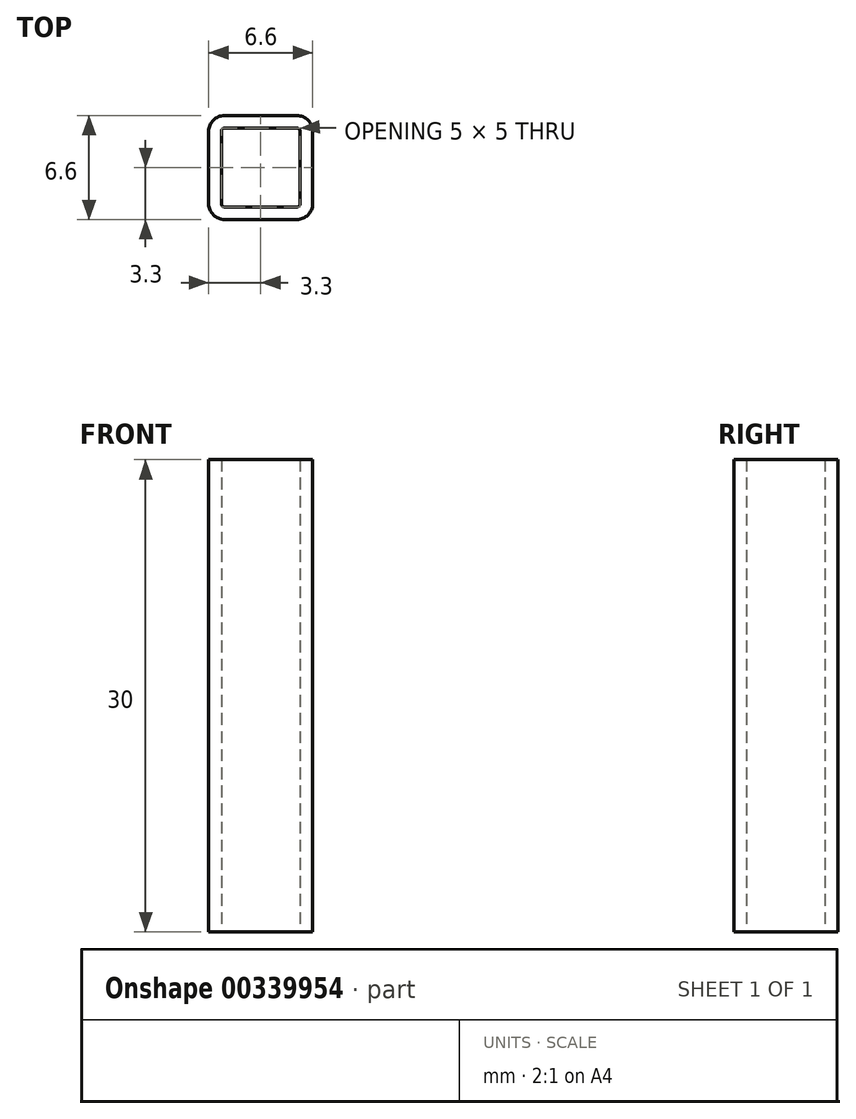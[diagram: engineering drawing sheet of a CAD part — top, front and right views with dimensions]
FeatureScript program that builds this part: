
annotation { "Feature Type Name" : "Feature", "Feature Type Description" : "" }
export const myFeature = defineFeature(function(context is Context, id is Id, definition is map)
    precondition{}
    {
        {
            var Q0;
            Q0=qCreatedBy(makeId("Top.planeOp"),FACE);
            var sketch = newSketch(context, id + "F0", { "sketchPlane" : qUnion([Q0])});
            skLineSegment(sketch, "E0.bottom", {"start": v(2.5, -2.5) * mm, "end": v(-2.5, -2.5) * mm});
            skLineSegment(sketch, "E0.top", {"start": v(2.5, 2.5) * mm, "end": v(-2.5, 2.5) * mm});
            skLineSegment(sketch, "E0.left", {"start": v(2.5, -2.5) * mm, "end": v(2.5, 2.5) * mm});
            skLineSegment(sketch, "E0.right", {"start": v(-2.5, -2.5) * mm, "end": v(-2.5, 2.5) * mm});
            skPoint(sketch, "E0.middle", {"position": v(0, 0) * mm});
            skLineSegment(sketch, "E1.bottom", {"start": v(-3.3, 3.3) * mm, "end": v(3.3, 3.3) * mm});
            skLineSegment(sketch, "E1.top", {"start": v(-3.3, -3.3) * mm, "end": v(3.3, -3.3) * mm});
            skLineSegment(sketch, "E1.left", {"start": v(-3.3, 3.3) * mm, "end": v(-3.3, -3.3) * mm});
            skLineSegment(sketch, "E1.right", {"start": v(3.3, 3.3) * mm, "end": v(3.3, -3.3) * mm});
            skSolve(sketch);
        }
        {
            var Q0;
            Q0 = qSketchRegion(id + "F0", true);
            extrude(context, id + "F1", {"entities" : qUnion([Q0]), "depth" : 30 * mm});
        }
        {
            var Q0;
            Q0=makeQuery(id+"F1.opExtrude","SWEPT_EDGE",EDGE,{"disambiguationData":[OSD([sQuery(id+"F0.wireOp",EDGE,"E0.bottom"),sQuery(id+"F0.wireOp",EDGE,"E0.right")])]});
            var Q1;
            Q1=makeQuery(id+"F1.opExtrude","SWEPT_EDGE",EDGE,{"disambiguationData":[OSD([sQuery(id+"F0.wireOp",EDGE,"E0.top"),sQuery(id+"F0.wireOp",EDGE,"E0.left")])]});
            var Q2;
            Q2=makeQuery(id+"F1.opExtrude","SWEPT_EDGE",EDGE,{"disambiguationData":[OSD([sQuery(id+"F0.wireOp",EDGE,"E0.bottom"),sQuery(id+"F0.wireOp",EDGE,"E0.left")])]});
            var Q3;
            Q3=makeQuery(id+"F1.opExtrude","SWEPT_EDGE",EDGE,{"disambiguationData":[OSD([sQuery(id+"F0.wireOp",EDGE,"E0.top"),sQuery(id+"F0.wireOp",EDGE,"E0.right")])]});
            fillet(context, id + "F2", {"entities" : qUnion([Q0, Q1, Q2, Q3]), "radius" : 0.2 * mm, "tangentPropagation" : true, "allowEdgeOverflow" : false});
        }
        {
            var Q0;
            Q0=makeQuery(id+"F1.opExtrude","SWEPT_EDGE",EDGE,{"disambiguationData":[OSD([sQuery(id+"F0.wireOp",EDGE,"E1.top"),sQuery(id+"F0.wireOp",EDGE,"E1.right")])]});
            var Q1;
            Q1=makeQuery(id+"F1.opExtrude","SWEPT_EDGE",EDGE,{"disambiguationData":[OSD([sQuery(id+"F0.wireOp",EDGE,"E1.bottom"),sQuery(id+"F0.wireOp",EDGE,"E1.right")])]});
            var Q2;
            Q2=makeQuery(id+"F1.opExtrude","SWEPT_EDGE",EDGE,{"disambiguationData":[OSD([sQuery(id+"F0.wireOp",EDGE,"E1.top"),sQuery(id+"F0.wireOp",EDGE,"E1.left")])]});
            var Q3;
            Q3=makeQuery(id+"F1.opExtrude","SWEPT_EDGE",EDGE,{"disambiguationData":[OSD([sQuery(id+"F0.wireOp",EDGE,"E1.bottom"),sQuery(id+"F0.wireOp",EDGE,"E1.left")])]});
            fillet(context, id + "F3", {"entities" : qUnion([Q0, Q1, Q2, Q3]), "radius" : 1 * mm, "tangentPropagation" : true, "allowEdgeOverflow" : false});
        }
    });
